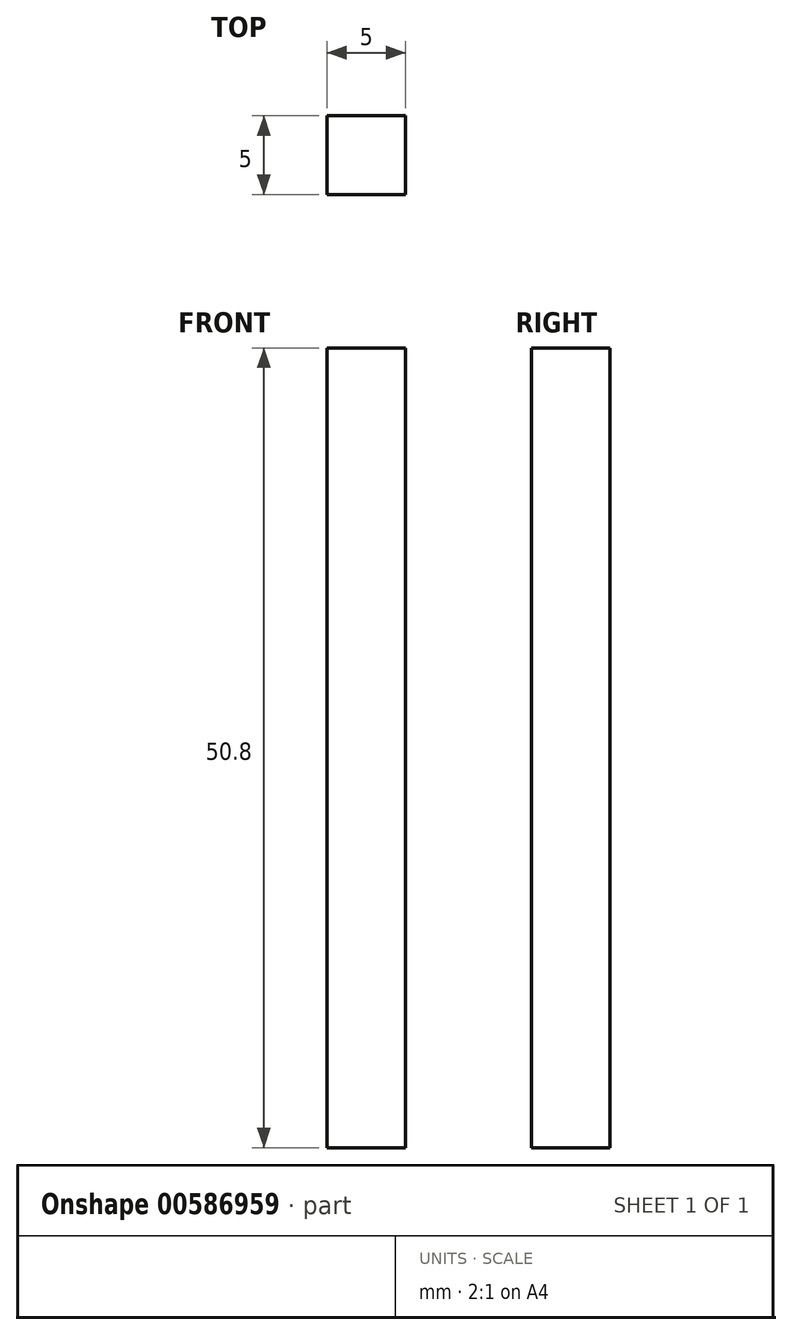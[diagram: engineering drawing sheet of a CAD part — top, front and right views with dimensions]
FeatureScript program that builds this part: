
annotation { "Feature Type Name" : "Feature", "Feature Type Description" : "" }
export const myFeature = defineFeature(function(context is Context, id is Id, definition is map)
    precondition{}
    {
        {
            var Q0;
            Q0=qCreatedBy(makeId("Top.planeOp"),FACE);
            var sketch = newSketch(context, id + "F0", { "sketchPlane" : qUnion([Q0])});
            skLineSegment(sketch, "E0.bottom", {"start": v(2.5, 2.5) * mm, "end": v(-2.5, 2.5) * mm});
            skLineSegment(sketch, "E0.top", {"start": v(2.5, -2.5) * mm, "end": v(-2.5, -2.5) * mm});
            skLineSegment(sketch, "E0.left", {"start": v(2.5, 2.5) * mm, "end": v(2.5, -2.5) * mm});
            skLineSegment(sketch, "E0.right", {"start": v(-2.5, 2.5) * mm, "end": v(-2.5, -2.5) * mm});
            skPoint(sketch, "E0.middle", {"position": v(0, 0) * mm});
            skSolve(sketch);
        }
        {
            var Q0;
            Q0=makeQuery(id+"F0.imprint","IMPRINT",FACE,{"disambiguationData":[TD([[makeQuery(id+"F0.imprint","IMPRINT",EDGE,{"derivedFrom":sQuery(id+"F0.wireOp",EDGE,"E0.bottom")}),1.0]])]});
            extrude(context, id + "F1", {"entities" : qUnion([Q0]), "depth" : 50.8 * mm, "offsetDistance" : 25.4 * mm});
        }
    });
